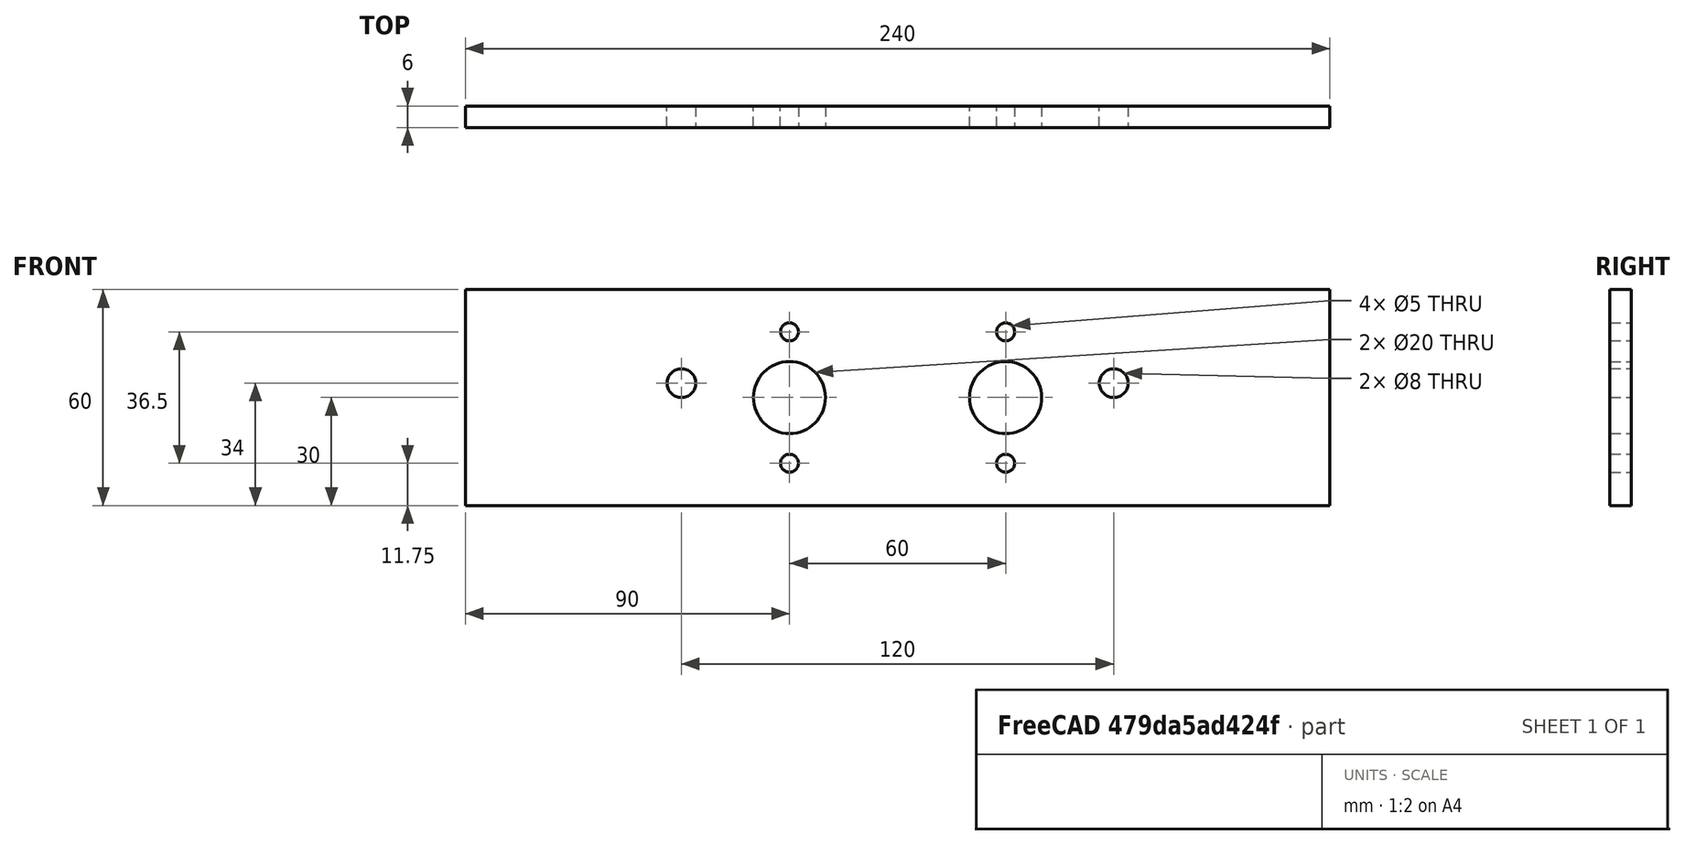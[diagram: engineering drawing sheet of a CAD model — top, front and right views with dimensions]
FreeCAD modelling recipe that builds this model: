
FCSTD DOCUMENT  (FreeCAD 0.18R4 (GitTag))
Label: soporte_rod1
License: All rights reserved
LicenseURL: http://en.wikipedia.org/wiki/All_rights_reserved
objects: Sketcher::SketchObject×1, PartDesign::Pad×1, PartDesign::Body×1
note: 4 computed .brp shape members not serialized (recipe doc carries the construction recipe); baked Part::Feature solids carry a one-line shape summary decoded from their .brp

FEATURE [Sketcher::SketchObject] Sketch
  MapMode = 5
  Placement = pos=(0,0,0) rot=(1,0,0;1.5708rad)
  Support = -> [XZ_Plane]
  sketch-geometry (12):
    g0: LineSegment StartX=0 StartY=0 StartZ=0 EndX=240 EndY=0 EndZ=0
    g1: LineSegment StartX=240 StartY=0 StartZ=0 EndX=240 EndY=60 EndZ=0
    g2: LineSegment StartX=240 StartY=60 StartZ=0 EndX=0 EndY=60 EndZ=0
    g3: LineSegment StartX=0 StartY=60 StartZ=0 EndX=0 EndY=0 EndZ=0
    g4: Circle CenterX=90 CenterY=30 CenterZ=0 NormalX=0 NormalY=0 NormalZ=1 AngleXU=0 Radius=10
    g5: Circle CenterX=150 CenterY=30 CenterZ=0 NormalX=0 NormalY=0 NormalZ=1 AngleXU=0 Radius=10
    g6: Circle CenterX=90 CenterY=11.75 CenterZ=0 NormalX=0 NormalY=0 NormalZ=1 AngleXU=0 Radius=2.5
    g7: Circle CenterX=90 CenterY=48.25 CenterZ=0 NormalX=0 NormalY=0 NormalZ=1 AngleXU=0 Radius=2.5
    g8: Circle CenterX=150 CenterY=48.25 CenterZ=0 NormalX=0 NormalY=0 NormalZ=1 AngleXU=0 Radius=2.5
    g9: Circle CenterX=150 CenterY=11.75 CenterZ=0 NormalX=0 NormalY=0 NormalZ=1 AngleXU=0 Radius=2.5
    g10: Circle CenterX=60 CenterY=34 CenterZ=0 NormalX=0 NormalY=0 NormalZ=1 AngleXU=0 Radius=4
    g11: Circle CenterX=180 CenterY=34 CenterZ=0 NormalX=0 NormalY=0 NormalZ=1 AngleXU=0 Radius=4
  constraints (35):
    c: Coincident(g0,g1)
    c: Coincident(g1,g2)
    c: Coincident(g2,g3)
    c: Coincident(g3,g0)
    c: Horizontal(g0)
    c: Horizontal(g2)
    c: Vertical(g1)
    c: Vertical(g3)
    c: Coincident(g0,g-1)
    c: DistanceX(g0,g0) = 240
    c: DistanceY(g3,g3) = 60
    c: Distance(g4,g3) = 90
    c: Radius(g4) = 10
    c: Equal(g4,g5) = 6
    c: Equal(g6,g7)
    c: Equal(g7,g8)
    c: Equal(g8,g9)
    c: Radius(g6) = 2.5
    c: Distance(g6,g7) = 36.5
    c: Distance(g8,g9) = 36.5
    c: Equal(g10,g11)
    c: Radius(g11) = 4
    c: Distance(g10,g2) = 26
    c: Distance(g10,g11) = 120
    c: Distance(g11,g2) = 26
    c: Distance(g10,g3) = 60
    c: DistanceX(g4,g5) = 60
    c: DistanceY(g6,g4) = 18.25
    c: Distance(g4,g2) = 30
    c: DistanceX(g4,g7) = 0
    c: DistanceX(g4,g6) = 0
    c: Distance(g5,g2) = 30
    c: DistanceY(g5,g8) = 18.25
    c: DistanceX(g8,g5) = 0
    c: DistanceX(g5,g9) = 0
FEATURE [PartDesign::Pad] Pad
  Length = 6
  Length2 = 100
  Placement = pos=(0,0,0) rot=(1,0,0;1.5708rad)
  Profile = -> Sketch
  Type = 0
FEATURE [PartDesign::Body] Body
  Group = -> [Sketch,Pad]
  Origin = -> Origin
  Tip = -> Pad
